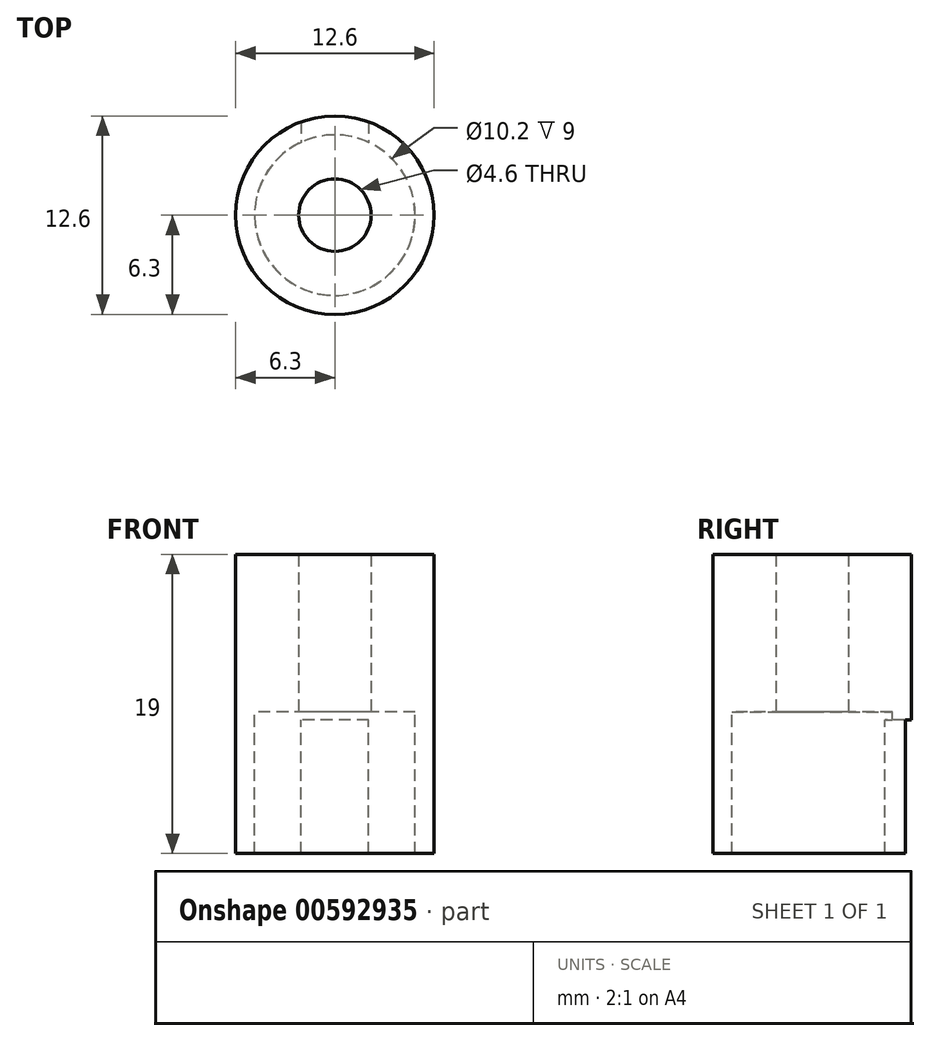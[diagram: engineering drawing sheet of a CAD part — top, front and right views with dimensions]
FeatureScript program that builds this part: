
annotation { "Feature Type Name" : "Feature", "Feature Type Description" : "" }
export const myFeature = defineFeature(function(context is Context, id is Id, definition is map)
    precondition{}
    {
        {
            var Q0;
            Q0=qCreatedBy(makeId("Top.planeOp"),FACE);
            var sketch = newSketch(context, id + "F0", { "sketchPlane" : qUnion([Q0])});
            skCircle(sketch, "E0", {"center": v(0, 0) * mm, "radius": 5.1 * mm});
            skCircle(sketch, "E1", {"center": v(0, 0) * mm, "radius": 6.3 * mm});
            skLineSegment(sketch, "E2.bottom", {"start": v(-2.15, 11.2) * mm, "end": v(2.15, 11.2) * mm});
            skLineSegment(sketch, "E2.top", {"start": v(-2.15, 4.62) * mm, "end": v(2.15, 4.62) * mm});
            skLineSegment(sketch, "E2.left", {"start": v(-2.15, 11.2) * mm, "end": v(-2.15, 4.62) * mm});
            skLineSegment(sketch, "E2.right", {"start": v(2.15, 11.2) * mm, "end": v(2.15, 4.62) * mm});
            skPoint(sketch, "E3", {"position": v(0, 4.62) * mm});
            skCircle(sketch, "E4", {"center": v(0, 0) * mm, "radius": 2.3 * mm});
            skCircle(sketch, "E5", {"center": v(0, 0) * mm, "radius": 1.15 * mm});
            skCircle(sketch, "E6", {"center": v(0, 0) * mm, "radius": 1.85 * mm});
            skSolve(sketch);
        }
        {
            var Q0;
            {var subQ0=sQuery(id+"F0.wireOp",EDGE,"E2.left");var subQ6=sQuery(id+"F0.wireOp",EDGE,"E1");var subQ7=makeQuery(id+"F0.imprint","INTERSECT",VERTEX,{"derivedFrom":[subQ6,subQ0]});Q0=makeQuery(id+"F0.imprint","IMPRINT",FACE,{"disambiguationData":[TD([[makeQuery(id+"F0.imprint","IMPRINT",EDGE,{"disambiguationData":[TD([[subQ7,-1.0]])],"derivedFrom":subQ6}),1.0]])]});}
            extrude(context, id + "F1", {"entities" : qUnion([Q0]), "oppositeDirection" : true, "depth" : 4 * mm, "offsetDistance" : 25 * mm});
        }
        {
            var Q0;
            {var subQ0=sQuery(id+"F0.wireOp",EDGE,"E2.left");var subQ6=sQuery(id+"F0.wireOp",EDGE,"E1");var subQ7=makeQuery(id+"F0.imprint","INTERSECT",VERTEX,{"derivedFrom":[subQ6,subQ0]});Q0=makeQuery(id+"F0.imprint","IMPRINT",FACE,{"disambiguationData":[TD([[makeQuery(id+"F0.imprint","IMPRINT",EDGE,{"disambiguationData":[TD([[subQ7,-1.0]])],"derivedFrom":subQ6}),1.0]])]});}
            var Q1;
            {var subQ0=sQuery(id+"F0.wireOp",EDGE,"E2.left");var subQ6=sQuery(id+"F0.wireOp",EDGE,"E1");var subQ7=makeQuery(id+"F0.imprint","INTERSECT",VERTEX,{"derivedFrom":[subQ6,subQ0]});Q1=makeQuery(id+"F0.imprint","IMPRINT",FACE,{"disambiguationData":[TD([[makeQuery(id+"F0.imprint","IMPRINT",EDGE,{"disambiguationData":[TD([[subQ7,1.0]])],"derivedFrom":subQ6}),1.0]])]});}
            var Q2;
            {var subQ0=sQuery(id+"F0.wireOp",EDGE,"E2.top");Q2=makeQuery(id+"F0.imprint","IMPRINT",FACE,{"disambiguationData":[TD([[makeQuery(id+"F0.imprint","IMPRINT",EDGE,{"derivedFrom":subQ0}),-1.0]])]});}
            var Q3;
            {var subQ0=sQuery(id+"F0.wireOp",EDGE,"E2.top");Q3=makeQuery(id+"F0.imprint","IMPRINT",FACE,{"disambiguationData":[TD([[makeQuery(id+"F0.imprint","IMPRINT",EDGE,{"derivedFrom":subQ0}),1.0]])]});}
            extrude(context, id + "F2", {"entities" : qUnion([Q0, Q1, Q2, Q3]), "operationType" : NewBodyOperationType.ADD, "depth" : 10 * mm, "offsetDistance" : 25 * mm});
        }
        {
            var Q0;
            {var subQ0=sQuery(id+"F0.wireOp",EDGE,"E2.left");var subQ6=sQuery(id+"F0.wireOp",EDGE,"E1");var subQ7=makeQuery(id+"F0.imprint","INTERSECT",VERTEX,{"derivedFrom":[subQ6,subQ0]});Q0=makeQuery(id+"F0.imprint","IMPRINT",FACE,{"disambiguationData":[TD([[makeQuery(id+"F0.imprint","IMPRINT",EDGE,{"disambiguationData":[TD([[subQ7,1.0]])],"derivedFrom":subQ6}),1.0]])]});}
            extrude(context, id + "F3", {"entities" : qUnion([Q0]), "operationType" : NewBodyOperationType.ADD, "oppositeDirection" : true, "depth" : 0.5 * mm, "offsetDistance" : 25 * mm});
        }
        {
            var Q0;
            Q0=makeQuery(id+"F1.opExtrude","CAP_FACE",FACE,{"disambiguationData":[OSD([sQuery(id+"F0.wireOp",EDGE,"E0"),sQuery(id+"F0.wireOp",EDGE,"E1"),sQuery(id+"F0.wireOp",EDGE,"E2.left"),sQuery(id+"F0.wireOp",EDGE,"E2.right")])],"isStart":false});
            extrude(context, id + "F4", {"entities" : qUnion([Q0]), "operationType" : NewBodyOperationType.ADD, "depth" : 5 * mm, "offsetDistance" : 25 * mm});
        }
    });
